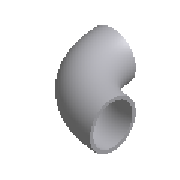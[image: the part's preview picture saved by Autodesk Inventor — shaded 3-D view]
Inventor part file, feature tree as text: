
AUTODESK INVENTOR PART (.ipt)
format: ipt  version: 2023.2 (Build 272271030, 271C)  size: 184,320 bytes
history: native  units: mm (DEFAULTED — no unit token found)
features: other x4, sketch x2, sweep x1
ambient origin geometry x8: Origin, YZ Plane, XZ Plane, XY Plane, X Axis, Y Axis, Z Axis, Center Point
bodies: Solid1 (feature_tree)
feature tree (7):
  sweep  "Sweep1"
  other  "Work Point1"
  other  "Work Point2"
  other  "Work Axis1"
  other  "Work Axis2"
  sketch  "Sketch1"  dims[d0=109.1mm d1=114.3mm]
  sketch  "Sketch2"  dims[d2=152.0mm d3=152.0mm d4=0.0mm d5=0.0mm]
